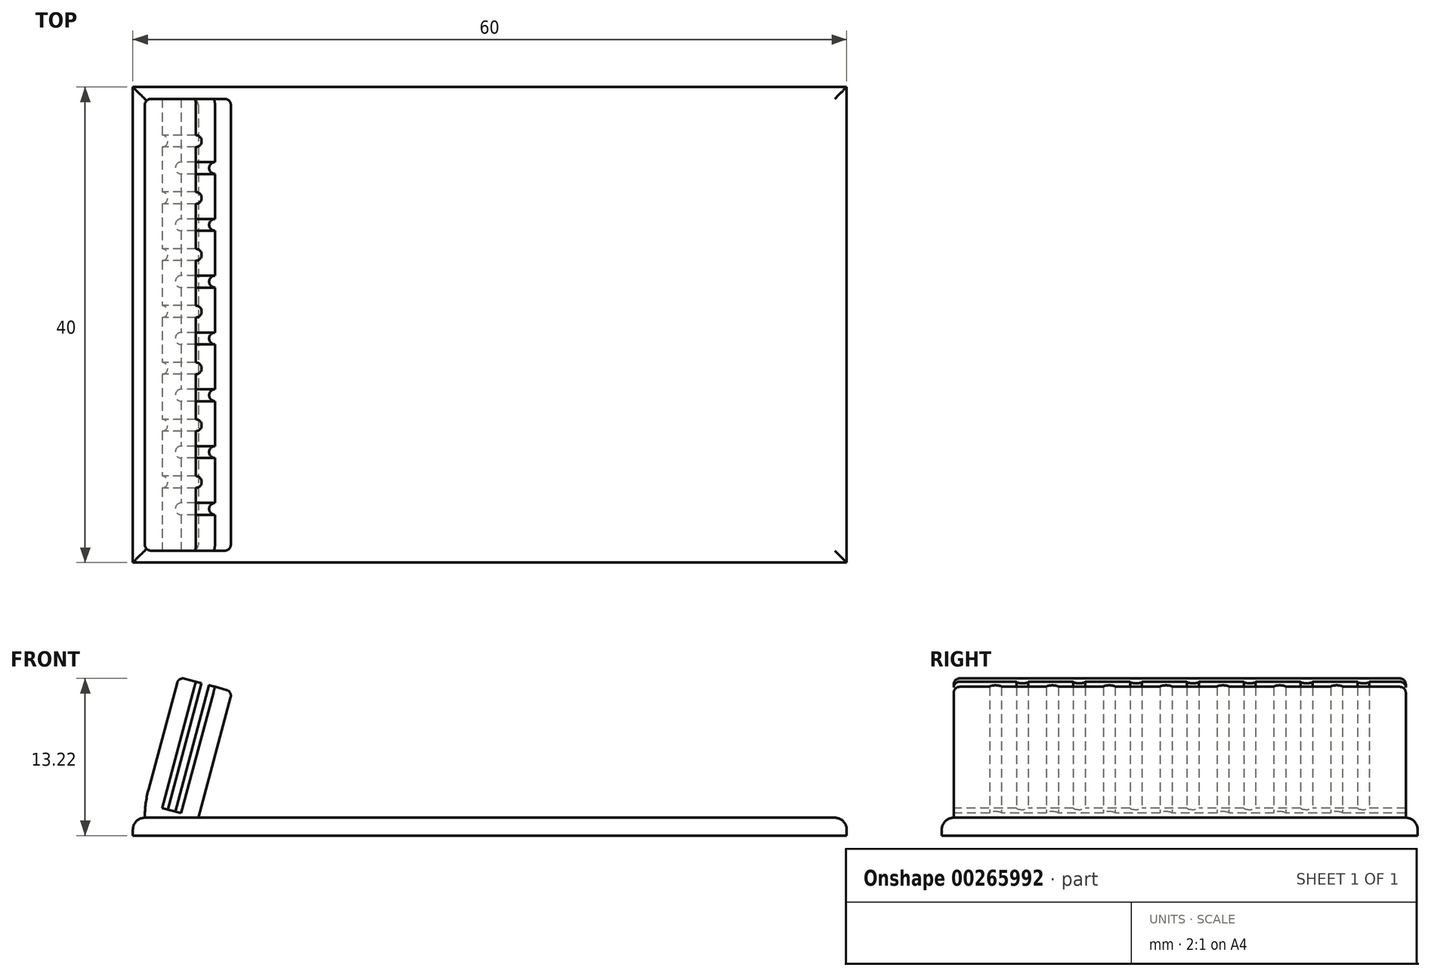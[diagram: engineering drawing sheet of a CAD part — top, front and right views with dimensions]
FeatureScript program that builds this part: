
annotation { "Feature Type Name" : "Feature", "Feature Type Description" : "" }
export const myFeature = defineFeature(function(context is Context, id is Id, definition is map)
    precondition{}
    {
        {
            var Q0;
            Q0=qCreatedBy(makeId("Top.planeOp"),FACE);
            var sketch = newSketch(context, id + "F0", { "sketchPlane" : qUnion([Q0])});
            skLineSegment(sketch, "E0.bottom", {"start": v(-30, 20) * mm, "end": v(30, 20) * mm});
            skLineSegment(sketch, "E0.top", {"start": v(-30, -20) * mm, "end": v(30, -20) * mm});
            skLineSegment(sketch, "E0.left", {"start": v(-30, 20) * mm, "end": v(-30, -20) * mm});
            skLineSegment(sketch, "E0.right", {"start": v(30, 20) * mm, "end": v(30, -20) * mm});
            skSolve(sketch);
        }
        {
            var Q0;
            Q0 = qSketchRegion(id + "F0", true);
            extrude(context, id + "F1", {"entities" : qUnion([Q0]), "depth" : 1.5 * mm});
        }
        {
            var Q0;
            Q0=makeQuery(id+"F1.opExtrude","CAP_FACE",FACE,{"disambiguationData":[OSD([sQuery(id+"F0.wireOp",EDGE,"E0.bottom"),sQuery(id+"F0.wireOp",EDGE,"E0.top"),sQuery(id+"F0.wireOp",EDGE,"E0.left"),sQuery(id+"F0.wireOp",EDGE,"E0.right")])],"isStart":false});
            var sketch = newSketch(context, id + "F2", { "sketchPlane" : qUnion([Q0])});
            skLineSegment(sketch, "E1.bottom", {"start": v(-29, 19) * mm, "end": v(-24.5, 19) * mm});
            skLineSegment(sketch, "E1.top", {"start": v(-29, -19) * mm, "end": v(-24.5, -19) * mm});
            skLineSegment(sketch, "E1.left", {"start": v(-29, 19) * mm, "end": v(-29, -19) * mm});
            skLineSegment(sketch, "E1.right", {"start": v(-24.5, 19) * mm, "end": v(-24.5, -19) * mm});
            skSolve(sketch);
        }
        {
            var Q0;
            Q0 = qSketchRegion(id + "F2", true);
            extrude(context, id + "F3", {"entities" : qUnion([Q0]), "operationType" : NewBodyOperationType.ADD, "depth" : 1.5 * mm});
        }
        {
            var Q0;
            Q0=makeQuery(id+"F3.opExtrude","CAP_EDGE",EDGE,{"disambiguationData":[OSD([sQuery(id+"F2.wireOp",EDGE,"E1.right")])],"isStart":false});
            chamfer(context, id + "F4", {"entities" : qUnion([Q0]), "chamferType" : ChamferType.OFFSET_ANGLE, "width" : 1.5 * mm, "oppositeDirection" : false, "angle" : 75 * degree, "tangentPropagation" : true});
        }
        {
            var Q0;
            Q0=makeQuery(id+"F4.opChamfer","BLEND_FACE",FACE,{"disambiguationData":[OSD([sQuery(id+"F2.wireOp",EDGE,"E1.right")])]});
            var sketch = newSketch(context, id + "F5", { "sketchPlane" : qUnion([Q0])});
            skLineSegment(sketch, "E2.0", {"start": v(-28.71, -19) * mm, "end": v(-28.71, 19) * mm});
            skLineSegment(sketch, "E2.1", {"start": v(-28.71, 19) * mm, "end": v(-27.21, 19) * mm});
            skLineSegment(sketch, "E2.2", {"start": v(-24.05, 19) * mm, "end": v(-24.05, -19) * mm});
            skLineSegment(sketch, "E2.3", {"start": v(-24.05, -19) * mm, "end": v(-25.55, -19) * mm});
            skLineSegment(sketch, "E3.left", {"start": v(-27.21, 19) * mm, "end": v(-27.21, 15.95) * mm});
            skLineSegment(sketch, "E3.right", {"start": v(-25.55, 19) * mm, "end": v(-25.55, 13.69) * mm});
            skArc(sketch, "E4", {"start": v(-27.21, 14.95) * mm, "mid": v(-26.71, 15.45) * mm, "end": v(-27.21, 15.95) * mm});
            skArc(sketch, "E5", {"start": v(-25.55, 13.69) * mm, "mid": v(-26.05, 13.19) * mm, "end": v(-25.55, 12.69) * mm});
            skArc(sketch, "E6.1.0.0", {"start": v(-27.21, 10.17) * mm, "mid": v(-26.71, 10.67) * mm, "end": v(-27.21, 11.17) * mm});
            skArc(sketch, "E6.1.0.1", {"start": v(-25.55, 8.91) * mm, "mid": v(-26.05, 8.41) * mm, "end": v(-25.55, 7.91) * mm});
            skArc(sketch, "E6.2.0.0", {"start": v(-27.21, 5.4) * mm, "mid": v(-26.71, 5.9) * mm, "end": v(-27.21, 6.4) * mm});
            skArc(sketch, "E6.2.0.1", {"start": v(-25.55, 4.13) * mm, "mid": v(-26.05, 3.63) * mm, "end": v(-25.55, 3.13) * mm});
            skArc(sketch, "E6.3.0.0", {"start": v(-27.21, 0.61) * mm, "mid": v(-26.71, 1.11) * mm, "end": v(-27.21, 1.61) * mm});
            skArc(sketch, "E6.3.0.1", {"start": v(-25.55, -0.65) * mm, "mid": v(-26.05, -1.15) * mm, "end": v(-25.55, -1.65) * mm});
            skArc(sketch, "E6.4.0.0", {"start": v(-27.21, -4.17) * mm, "mid": v(-26.71, -3.67) * mm, "end": v(-27.21, -3.17) * mm});
            skArc(sketch, "E6.4.0.1", {"start": v(-25.55, -5.43) * mm, "mid": v(-26.05, -5.93) * mm, "end": v(-25.55, -6.43) * mm});
            skArc(sketch, "E6.5.0.0", {"start": v(-27.21, -8.95) * mm, "mid": v(-26.71, -8.45) * mm, "end": v(-27.21, -7.95) * mm});
            skArc(sketch, "E6.5.0.1", {"start": v(-25.55, -10.2) * mm, "mid": v(-26.05, -10.7) * mm, "end": v(-25.55, -11.2) * mm});
            skArc(sketch, "E6.6.0.0", {"start": v(-27.21, -13.73) * mm, "mid": v(-26.71, -13.23) * mm, "end": v(-27.21, -12.73) * mm});
            skArc(sketch, "E6.6.0.1", {"start": v(-25.55, -14.99) * mm, "mid": v(-26.05, -15.49) * mm, "end": v(-25.55, -15.99) * mm});
            skLineSegment(sketch, "E6.direction1", {"start": v(-27.21, 14.95) * mm, "end": v(-27.21, 11.17) * mm, "construction": true});
            skLineSegment(sketch, "E7.trimOffspring", {"start": v(-25.55, 12.69) * mm, "end": v(-25.55, 8.91) * mm});
            skLineSegment(sketch, "E8.trimOffspring", {"start": v(-25.55, 7.91) * mm, "end": v(-25.55, 4.13) * mm});
            skLineSegment(sketch, "E9.trimOffspring", {"start": v(-25.55, 3.13) * mm, "end": v(-25.55, -0.65) * mm});
            skLineSegment(sketch, "E10.trimOffspring", {"start": v(-25.55, -1.65) * mm, "end": v(-25.55, -5.43) * mm});
            skLineSegment(sketch, "E11.trimOffspring", {"start": v(-25.55, -6.43) * mm, "end": v(-25.55, -10.2) * mm});
            skLineSegment(sketch, "E12.trimOffspring", {"start": v(-25.55, -11.2) * mm, "end": v(-25.55, -14.99) * mm});
            skLineSegment(sketch, "E13.trimOffspring", {"start": v(-25.55, -15.99) * mm, "end": v(-25.55, -19) * mm});
            skLineSegment(sketch, "E14.trimOffspring", {"start": v(-27.21, -13.73) * mm, "end": v(-27.21, -19) * mm});
            skLineSegment(sketch, "E15.trimOffspring", {"start": v(-27.21, -8.95) * mm, "end": v(-27.21, -12.73) * mm});
            skLineSegment(sketch, "E16.trimOffspring", {"start": v(-27.21, -4.17) * mm, "end": v(-27.21, -7.95) * mm});
            skLineSegment(sketch, "E17.trimOffspring", {"start": v(-27.21, 0.61) * mm, "end": v(-27.21, -3.17) * mm});
            skLineSegment(sketch, "E18.trimOffspring", {"start": v(-27.21, 5.4) * mm, "end": v(-27.21, 1.61) * mm});
            skLineSegment(sketch, "E19.trimOffspring", {"start": v(-27.21, 10.17) * mm, "end": v(-27.21, 6.4) * mm});
            skLineSegment(sketch, "E20.trimOffspring", {"start": v(-27.21, 14.95) * mm, "end": v(-27.21, 11.17) * mm});
            skLineSegment(sketch, "E21.trimOffspring", {"start": v(-25.55, 19) * mm, "end": v(-24.05, 19) * mm});
            skLineSegment(sketch, "E22.trimOffspring", {"start": v(-27.21, -19) * mm, "end": v(-28.71, -19) * mm});
            skSolve(sketch);
        }
        {
            var Q0;
            Q0 = qSketchRegion(id + "F5", true);
            extrude(context, id + "F6", {"entities" : qUnion([Q0]), "operationType" : NewBodyOperationType.ADD, "depth" : 11 * mm});
        }
        {
            var Q0;
            Q0=makeQuery(id+"F1.opExtrude","CAP_EDGE",EDGE,{"disambiguationData":[OSD([sQuery(id+"F0.wireOp",EDGE,"E0.top")])],"isStart":false});
            var Q1;
            Q1=makeQuery(id+"F1.opExtrude","CAP_EDGE",EDGE,{"disambiguationData":[OSD([sQuery(id+"F0.wireOp",EDGE,"E0.right")])],"isStart":false});
            var Q2;
            Q2=makeQuery(id+"F1.opExtrude","CAP_EDGE",EDGE,{"disambiguationData":[OSD([sQuery(id+"F0.wireOp",EDGE,"E0.bottom")])],"isStart":false});
            var Q3;
            Q3=makeQuery(id+"F1.opExtrude","CAP_EDGE",EDGE,{"disambiguationData":[OSD([sQuery(id+"F0.wireOp",EDGE,"E0.left")])],"isStart":false});
            fillet(context, id + "F7", {"entities" : qUnion([Q0, Q1, Q2, Q3]), "radius" : 1 * mm, "tangentPropagation" : true, "allowEdgeOverflow" : false});
        }
        {
            var Q0;
            Q0=makeQuery(id+"F6.boolean.opBoolean","MERGE",EDGE,{"derivedFrom":[makeQuery(id+"F4.opChamfer","BLEND_EDGE",EDGE,{"blendedFrom":[makeQuery(id+"F3.opExtrude","CAP_EDGE",EDGE,{"disambiguationData":[OSD([sQuery(id+"F2.wireOp",EDGE,"E1.right")])],"isStart":false}),makeQuery(id+"F3.opExtrude","SWEPT_FACE",FACE,{"disambiguationData":[OSD([sQuery(id+"F2.wireOp",EDGE,"E1.left")])]})],"blendedInto":[makeQuery(id+"F3.opExtrude","SWEPT_FACE",FACE,{"disambiguationData":[OSD([sQuery(id+"F2.wireOp",EDGE,"E1.left")])]})]}),makeQuery(id+"F6.opExtrude","CAP_EDGE",EDGE,{"disambiguationData":[OSD([sQuery(id+"F5.wireOp",EDGE,"E2.0")])],"isStart":true})]});
            fillet(context, id + "F8", {"entities" : qUnion([Q0]), "radius" : 9 * mm, "tangentPropagation" : true, "allowEdgeOverflow" : false});
        }
        {
            var Q0;
            Q0=makeQuery(id+"F6.opExtrude","CAP_EDGE",EDGE,{"disambiguationData":[OSD([sQuery(id+"F5.wireOp",EDGE,"E22.trimOffspring")])],"isStart":false});
            var Q1;
            Q1=makeQuery(id+"F6.opExtrude","CAP_EDGE",EDGE,{"disambiguationData":[OSD([sQuery(id+"F5.wireOp",EDGE,"E2.3")])],"isStart":false});
            var Q2;
            Q2=makeQuery(id+"F6.opExtrude","CAP_EDGE",EDGE,{"disambiguationData":[OSD([sQuery(id+"F5.wireOp",EDGE,"E21.trimOffspring")])],"isStart":false});
            var Q3;
            Q3=makeQuery(id+"F6.opExtrude","CAP_EDGE",EDGE,{"disambiguationData":[OSD([sQuery(id+"F5.wireOp",EDGE,"E2.1")])],"isStart":false});
            var Q4;
            Q4=makeQuery(id+"F6.opExtrude","CAP_EDGE",EDGE,{"disambiguationData":[OSD([sQuery(id+"F5.wireOp",EDGE,"E2.0")])],"isStart":false});
            var Q5;
            Q5=makeQuery(id+"F6.opExtrude","CAP_EDGE",EDGE,{"disambiguationData":[OSD([sQuery(id+"F5.wireOp",EDGE,"E2.2")])],"isStart":false});
            var Q6;
            Q6=makeQuery(id+"F6.opExtrude","SWEPT_EDGE",EDGE,{"disambiguationData":[OSD([sQuery(id+"F5.wireOp",EDGE,"E2.2"),sQuery(id+"F5.wireOp",EDGE,"E2.3")])]});
            var Q7;
            Q7=makeQuery(id+"F6.opExtrude","SWEPT_EDGE",EDGE,{"disambiguationData":[OSD([sQuery(id+"F5.wireOp",EDGE,"E2.0"),sQuery(id+"F5.wireOp",EDGE,"E22.trimOffspring")])]});
            var Q8;
            Q8=makeQuery(id+"F6.opExtrude","SWEPT_EDGE",EDGE,{"disambiguationData":[OSD([sQuery(id+"F5.wireOp",EDGE,"E2.0"),sQuery(id+"F5.wireOp",EDGE,"E2.1")])]});
            var Q9;
            Q9=makeQuery(id+"F6.opExtrude","SWEPT_EDGE",EDGE,{"disambiguationData":[OSD([sQuery(id+"F5.wireOp",EDGE,"E2.2"),sQuery(id+"F5.wireOp",EDGE,"E21.trimOffspring")])]});
            fillet(context, id + "F9", {"entities" : qUnion([Q0, Q1, Q2, Q3, Q4, Q5, Q6, Q7, Q8, Q9]), "radius" : 0.5 * mm, "tangentPropagation" : true, "allowEdgeOverflow" : false});
        }
    });
